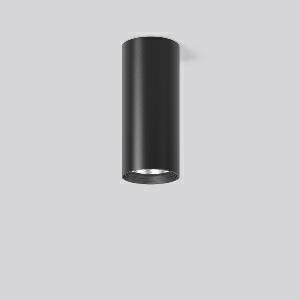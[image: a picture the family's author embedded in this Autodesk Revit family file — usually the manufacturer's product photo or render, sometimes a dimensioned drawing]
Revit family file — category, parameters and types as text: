
# Revit family: heledon_mini_a_931209_003_76_de56
name_source: partatom
category: Lighting Fixtures
units: mm (PartAtom-declared; Revit-internal decimal feet)

## family parameters
Cut with Voids When Loaded = No
Host = Face
Light Source = No
Part Type = Normal
Room Calculation Point = No
Round Connector Dimension = Use Diameter
Shared = No

## types (1)
- HELEDON mini A (1 x LED Modul 930, 3500 lm, 3000)
    Apparent Load = 29 VA
    Approval mark = CE
    CIE Flux Codes = 99 100 100 100 100
    Color Rendering = 90
    Color Temperature = 3000
    Default Elevation = 1800 mm
    Description = Series: HELEDON mini
Cylindrical surface-mounted downlight. Housing: die-cast aluminium, powder-coated. Internal ceiling frame polycarbonate with bayonet mounting. Black plastic ring and recessed LED to prevent glare from the side. Optical assembly with reflector made of MIRO-Silver with 98% total light reflection for outstanding efficiency - can be changed without tools. Best colour rendering index Ra>90. Suitable for Ceiling mounting. Easy installation with a separate ceiling frame with bayonet mounting and plug connection. Driver integrated. Connected via plug-in connector. High quality converter without flickering and stroboscopic effect. The following accessories can be mounted without use of tools: interchangeable lenses, decorative glasses, honeycomb louvre, clear and frosted diffusers, white interchangeable plastic ring. 
Colour: deep black, matt (RAL 9005)
Diameter: 87 mm
Height: 197 mm
Lamp: LED
Socket: without socket
Colour temperature: 3000K
Colour rendering index (CRI): 92
System power: 29 W
Rated luminous flux: 3500 lm
Luminous efficiency: 121 lm/W
Control gear: Converter, dimmable, DALI
Protection class: I
Type of protection: IP 20
    Height = 197 mm
    Lamp = 1 x LED Modul 930
    Lamp Light Flux = 3500 lm
    Lamp count = 1
    Length = 87 mm
    Lifetime = 50000 h
    Luminous efficacy = 121 lm/W
    Manufacturer = RZB
    ModVariant = No
    Model = 931209.003.76
    Mounting Place = Ceiling
    Mounting Type = Surface mounted
    Number of Poles = 1
    OnlyDefault = Yes
    Power Factor = 1
    Product Name = HELEDON mini A
    Product group = Surface mounted downlights
    ProductGroupID = 302
    Protection Class = Protection class I
    Protection Degree = IP 20
    RLX_Detail_Level = 1
    RLX_Emergency_Light_Flux = 0 lm
    RLX_Emergency_Type = 0
    RLX_Emergency_Type_DB = No
    RlxData = <blob elided: 106997 chars, md5=35f6abd2>
    Socket = socket
    Standby Power = 0 W
    System Light Flux = 3500 lm
    System Power = 29 W
    Type Comments = Product without accessories
    Type Image = 931188.003.jpg
    URL = http://relux.com
    VarID = ---
    Voltage = 230 V
    Voltage Range = 220-240 V
    Weight = 0.00 kg
    Width = 0 mm  [stored 0 ft]

note: [stored X ft] marks values corroborated as IEEE doubles in the binary element streams (Revit-internal decimal feet)

## geometry (parser evidence)
native form markers: Blend x4, Sweep x11
no freeform markers — native parametric forms only
